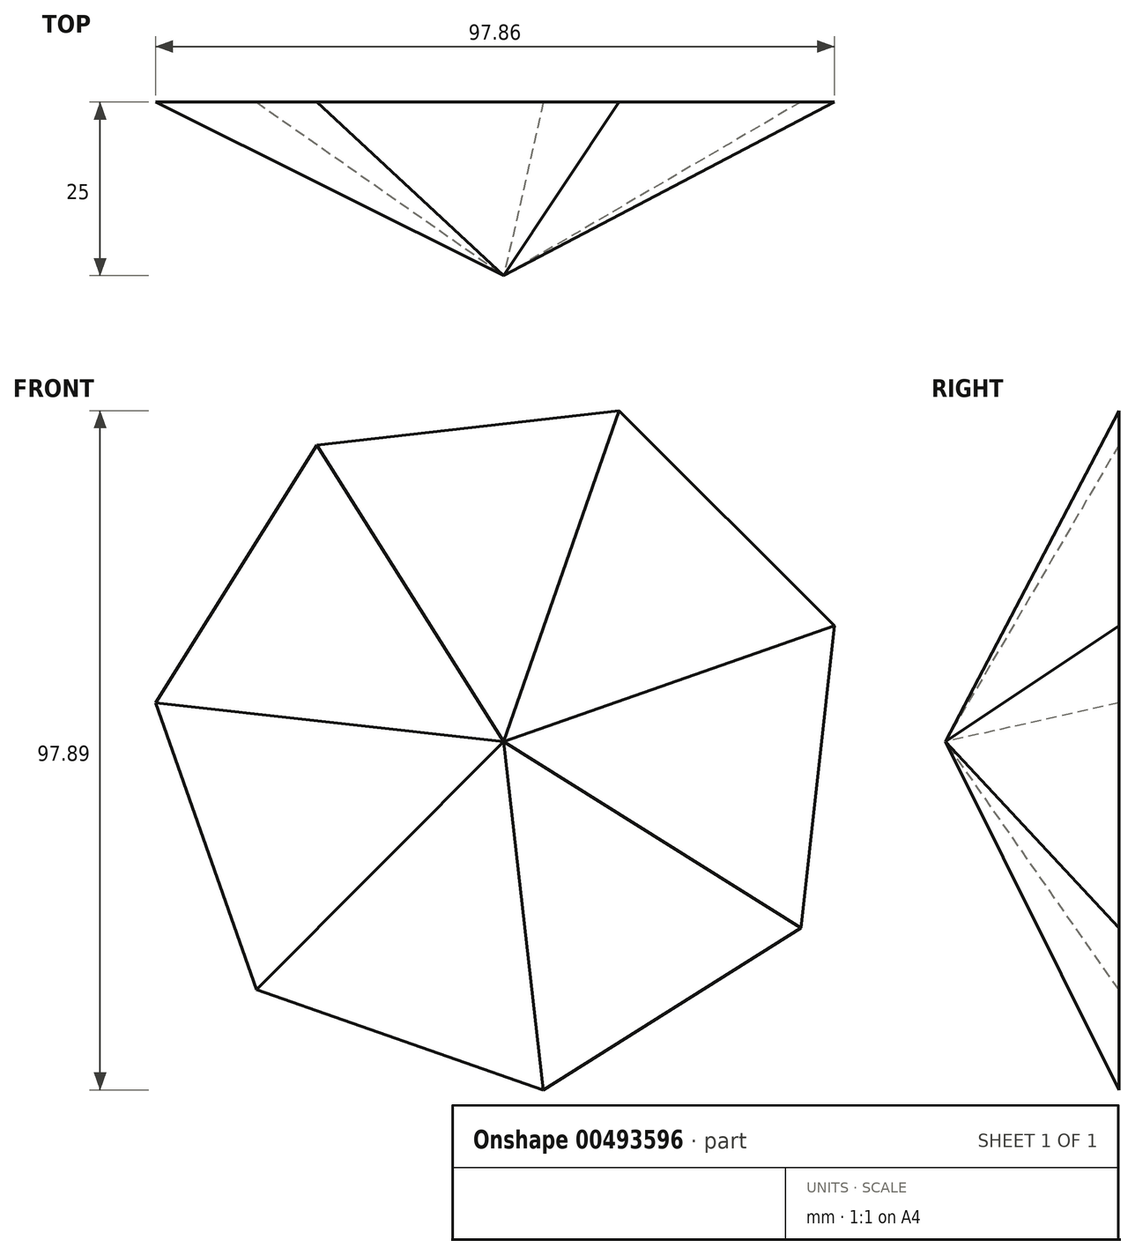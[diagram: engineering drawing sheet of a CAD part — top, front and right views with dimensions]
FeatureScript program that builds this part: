
annotation { "Feature Type Name" : "Feature", "Feature Type Description" : "" }
export const myFeature = defineFeature(function(context is Context, id is Id, definition is map)
    precondition{}
    {
        {
            var Q0;
            Q0=qCreatedBy(makeId("Front.planeOp"),FACE);
            var sketch = newSketch(context, id + "F0", { "sketchPlane" : qUnion([Q0])});
            skCircle(sketch, "E0.cCircle", {"center": v(0, 0) * mm, "radius": 50.52 * mm, "construction": true});
            skLineSegment(sketch, "E0.0", {"start": v(-50.2, 5.6) * mm, "end": v(-26.93, 42.74) * mm});
            skLineSegment(sketch, "E0.1", {"start": v(-26.93, 42.74) * mm, "end": v(16.63, 47.7) * mm});
            skLineSegment(sketch, "E0.2", {"start": v(16.63, 47.7) * mm, "end": v(47.66, 16.74) * mm});
            skLineSegment(sketch, "E0.3", {"start": v(47.66, 16.74) * mm, "end": v(42.8, -26.82) * mm});
            skLineSegment(sketch, "E0.4", {"start": v(42.8, -26.82) * mm, "end": v(5.72, -50.2) * mm});
            skLineSegment(sketch, "E0.5", {"start": v(5.72, -50.2) * mm, "end": v(-35.68, -35.76) * mm});
            skLineSegment(sketch, "E0.6", {"start": v(-35.68, -35.76) * mm, "end": v(-50.2, 5.6) * mm});
            skSolve(sketch);
        }
        {
            var Q0;
            Q0=qCreatedBy(makeId("Front.planeOp"),FACE);
            cPlane(context, id + "F1", {"entities" : qUnion([Q0]), "cplaneType" : CPlaneType.OFFSET, "offset" : 25 * mm, "width" : 150 * mm, "height" : 150 * mm});
        }
        {
            var Q0;
            Q0=qCreatedBy(id+"F1.planeOp",FACE);
            var sketch = newSketch(context, id + "F2", { "sketchPlane" : qUnion([Q0])});
            skPoint(sketch, "E1", {"position": v(0, 0) * mm});
            skSolve(sketch);
        }
        {
            var Q0;
            Q0=makeQuery(id+"F0.imprint","IMPRINT",FACE,{"disambiguationData":[TD([[makeQuery(id+"F0.imprint","IMPRINT",EDGE,{"derivedFrom":sQuery(id+"F0.wireOp",EDGE,"E0.0")}),-1.0]])]});
            var Q1;
            Q1=sQuery(id+"F2.wireOp",VERTEX,"E1");
            loft(context, id + "F3", {"sheetProfilesArray" : [{ "sheetProfileEntities" : qUnion([Q0]) }, { "sheetProfileEntities" : qUnion([Q1]) }]});
        }
    });
